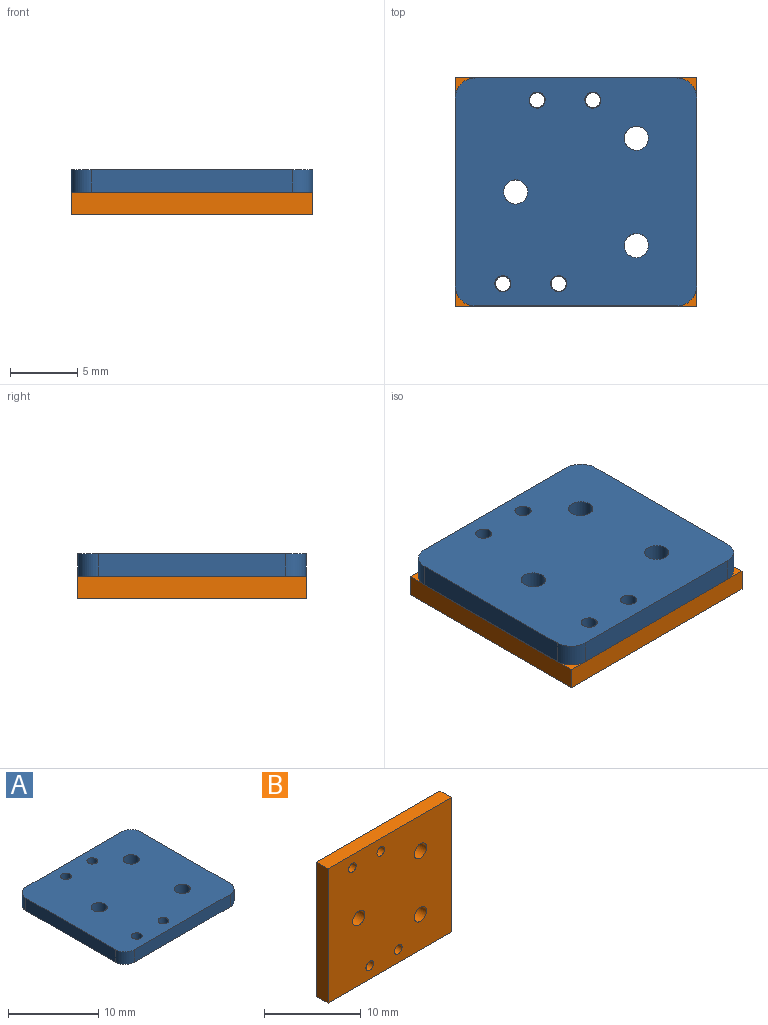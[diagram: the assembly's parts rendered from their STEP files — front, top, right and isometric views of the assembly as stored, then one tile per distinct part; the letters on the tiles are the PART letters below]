
ASSEMBLY  parts=2 mates=1
PART A: 17 faces, bbox 18x17x1.7 mm
  f0: cylinder r=0.6mm len=1.7mm, axis (0,0,1), area 6.4mm2, adj f7,f12
  f1: cylinder r=0.6mm len=1.7mm, axis (0,0,1), area 6.4mm2, adj f7,f12
  f2: cylinder r=0.6mm len=1.7mm, axis (0,0,1), area 6.4mm2, adj f7,f12
  f3: cylinder r=0.6mm len=1.7mm, axis (0,0,1), area 6.4mm2, adj f7,f12
  f4: cylinder r=0.9mm len=1.8mm, axis (0,0,-1), area 9.6mm2, adj f7,f12
  f5: cylinder r=0.9mm len=1.8mm, axis (0,0,-1), area 9.6mm2, adj f7,f12
  f6: cylinder r=0.9mm len=1.8mm, axis (0,0,-1), area 9.6mm2, adj f7,f12
  f7: plane 18x17mm, normal (0,0,1), area 291.9mm2, adj f0,f1,f2,f3,f4,f5,f6,f8
  f8: plane 14x1.7mm, normal (-1,0,0), area 23.8mm2, adj f7,f12,f13,f15
  f9: plane 15x1.7mm, normal (0,-1,0), area 25.5mm2, adj f7,f12,f15,f16
  f10: plane 14x1.7mm, normal (1,0,0), area 23.8mm2, adj f7,f12,f14,f16
  f11: plane 15x1.7mm, normal (0,1,0), area 25.5mm2, adj f7,f12,f13,f14
  f12: plane 18x17mm, normal (0,0,-1), area 291.9mm2, adj f0,f1,f2,f3,f4,f5,f6,f8
  f13: cylinder r=1.5mm len=1.7mm, axis (0,0,-1), area 4mm2, adj f7,f8,f11,f12
  f14: cylinder r=1.5mm len=1.7mm, axis (0,0,-1), area 4mm2, adj f7,f10,f11,f12
  f15: cylinder r=1.5mm len=1.7mm, axis (0,0,-1), area 4mm2, adj f7,f8,f9,f12
  f16: cylinder r=1.5mm len=1.7mm, axis (0,0,-1), area 4mm2, adj f7,f9,f10,f12
PART B: 13 faces, bbox 18x1.6x17 mm
  f0: plane 18x1.65mm, normal (0,0,-1), area 29.6mm2, adj f1,f3,f11,f12
  f1: plane 17x1.65mm, normal (1,0,0), area 28mm2, adj f0,f2,f11,f12
  f2: plane 18x1.65mm, normal (0,0,1), area 29.6mm2, adj f1,f3,f11,f12
  f3: plane 17x1.65mm, normal (-1,0,0), area 28mm2, adj f0,f2,f11,f12
  f4: cylinder r=0.56mm len=1.65mm, axis (0,1,0), area 5.8mm2, adj f11,f12
  f5: cylinder r=0.56mm len=1.65mm, axis (0,1,0), area 5.8mm2, adj f11,f12
  f6: cylinder r=0.9mm len=1.8mm, axis (0,1,0), area 9.3mm2, adj f11,f12
  f7: cylinder r=0.56mm len=1.65mm, axis (0,1,0), area 5.8mm2, adj f11,f12
  f8: cylinder r=0.9mm len=1.8mm, axis (0,1,0), area 9.3mm2, adj f11,f12
  f9: cylinder r=0.56mm len=1.65mm, axis (0,1,0), area 5.8mm2, adj f11,f12
  f10: cylinder r=0.9mm len=1.8mm, axis (0,1,0), area 9.3mm2, adj f11,f12
  f11: plane 18x17mm, normal (0,1,0), area 294.4mm2, adj f0,f1,f2,f3,f4,f5,f6,f7
  f12: plane 18x17mm, normal (0,-1,0), area 294.4mm2, adj f0,f1,f2,f3,f4,f5,f6,f7
PLACE A t=(-0.26,-0.5,3.6)mm
PLACE B rot(axis=(1,0,0),90deg) t=(-0.26,16.5,1.95)mm
MATE fastened B.f8 <-> A.f5  axis (0,0,1) through (13.24,12,3.6)mm
